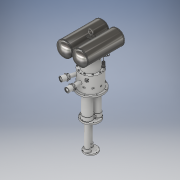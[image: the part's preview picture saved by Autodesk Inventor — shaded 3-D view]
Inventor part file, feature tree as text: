
AUTODESK INVENTOR PART (.ipt)
format: ipt  version: 2018 (Build 220112000, 112)  size: 2,113,024 bytes
history: native  units: in
note: dims shown in document units (in); Inventor stores cm internally (conversion verified against a paired STEP export)
features: extrude x1, sketch x1
ambient origin geometry x8: Origin, YZ Plane, XZ Plane, XY Plane, X Axis, Y Axis, Z Axis, Center Point
bodies: Solid2 (feature_tree), Solid1 (feature_tree)
feature tree (2):
  extrude  "Extrusion1"  [1 undecoded]
  sketch  "Sketch1"  dims[d0=3.6875in d1=0.0in]
note: 1 required parameter value undecoded (feature->parameter linkage not recoverable at this tier; creation-order binding heuristic only, values carry confidence <= 0.55)
